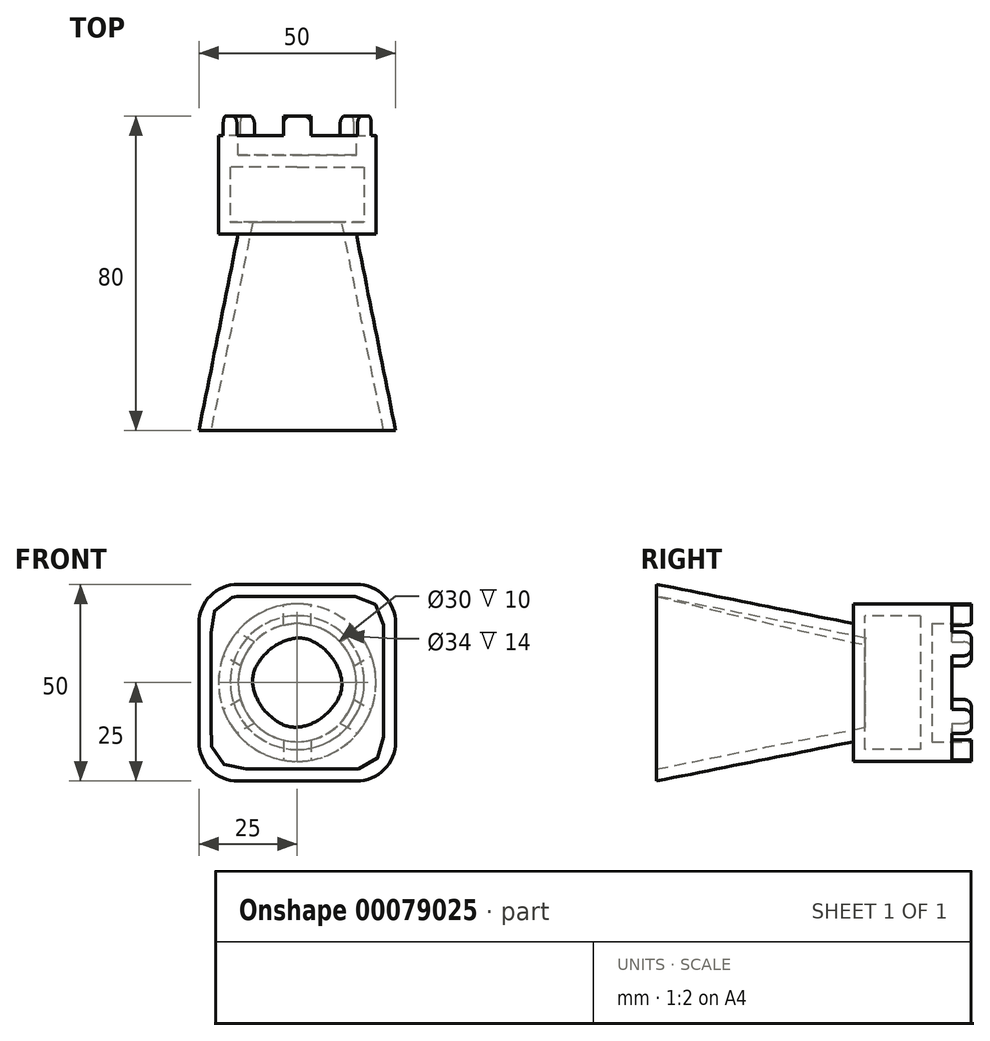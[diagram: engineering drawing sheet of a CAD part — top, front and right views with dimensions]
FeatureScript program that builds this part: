
annotation { "Feature Type Name" : "Feature", "Feature Type Description" : "" }
export const myFeature = defineFeature(function(context is Context, id is Id, definition is map)
    precondition{}
    {
        {
            var Q0;
            Q0=qCreatedBy(makeId("Front.planeOp"),FACE);
            var sketch = newSketch(context, id + "F0", { "sketchPlane" : qUnion([Q0])});
            skCircle(sketch, "E0", {"center": v(0, 0) * mm, "radius": 20 * mm});
            skSolve(sketch);
        }
        {
            var Q0;
            Q0=makeQuery(id+"F0.imprint","IMPRINT",FACE,{"disambiguationData":[TD([[makeQuery(id+"F0.imprint","IMPRINT",EDGE,{"derivedFrom":sQuery(id+"F0.wireOp",EDGE,"E0")}),1.0]])]});
            extrude(context, id + "F1", {"entities" : qUnion([Q0]), "oppositeDirection" : true, "depth" : 30 * mm});
        }
        {
            var Q0;
            Q0=makeQuery(id+"F1.opExtrude","CAP_FACE",FACE,{"disambiguationData":[OSD([sQuery(id+"F0.wireOp",EDGE,"E0")])],"isStart":false});
            var sketch = newSketch(context, id + "F2", { "sketchPlane" : qUnion([Q0])});
            skCircle(sketch, "E1", {"center": v(0, 0) * mm, "radius": 15 * mm});
            skSolve(sketch);
        }
        {
            var Q0;
            Q0 = qSketchRegion(id + "F2", true);
            extrude(context, id + "F3", {"entities" : qUnion([Q0]), "operationType" : NewBodyOperationType.REMOVE, "oppositeDirection" : true, "depth" : 10 * mm});
        }
        {
            var Q0;
            Q0=makeQuery(id+"F1.opExtrude","CAP_FACE",FACE,{"disambiguationData":[OSD([sQuery(id+"F0.wireOp",EDGE,"E0")])],"isStart":false});
            var sketch = newSketch(context, id + "F4", { "sketchPlane" : qUnion([Q0])});
            skLineSegment(sketch, "E2.bottom", {"start": v(-3.5, -14.59) * mm, "end": v(3.5, -14.59) * mm});
            skLineSegment(sketch, "E2.top", {"start": v(-3.5, -19.7) * mm, "end": v(3.5, -19.7) * mm, "construction": true});
            skLineSegment(sketch, "E2.left", {"start": v(-3.5, -14.59) * mm, "end": v(-3.5, -19.7) * mm});
            skLineSegment(sketch, "E2.right", {"start": v(3.5, -14.59) * mm, "end": v(3.5, -19.7) * mm});
            skLineSegment(sketch, "E3", {"start": v(0, -19.7) * mm, "end": v(0, 0) * mm, "construction": true});
            skArc(sketch, "E4", {"start": v(-3.5, -19.7) * mm, "mid": v(0, -20) * mm, "end": v(3.5, -19.7) * mm});
            skLineSegment(sketch, "E5.1.0", {"start": v(10.88, -10.32) * mm, "end": v(15.3, -12.88) * mm});
            skLineSegment(sketch, "E5.1.1", {"start": v(10.88, -10.32) * mm, "end": v(14.38, -4.26) * mm});
            skLineSegment(sketch, "E5.1.2", {"start": v(15.3, -12.88) * mm, "end": v(18.8, -6.81) * mm, "construction": true});
            skLineSegment(sketch, "E5.1.3", {"start": v(14.38, -4.26) * mm, "end": v(18.8, -6.81) * mm});
            skArc(sketch, "E5.1.4", {"start": v(15.3, -12.88) * mm, "mid": v(17.32, -10) * mm, "end": v(18.8, -6.81) * mm});
            skLineSegment(sketch, "E5.2.0", {"start": v(14.38, 4.26) * mm, "end": v(18.8, 6.81) * mm});
            skLineSegment(sketch, "E5.2.1", {"start": v(14.38, 4.26) * mm, "end": v(10.88, 10.32) * mm});
            skLineSegment(sketch, "E5.2.2", {"start": v(18.8, 6.81) * mm, "end": v(15.3, 12.88) * mm, "construction": true});
            skLineSegment(sketch, "E5.2.3", {"start": v(10.88, 10.32) * mm, "end": v(15.3, 12.88) * mm});
            skArc(sketch, "E5.2.4", {"start": v(18.8, 6.81) * mm, "mid": v(17.32, 10) * mm, "end": v(15.3, 12.88) * mm});
            skLineSegment(sketch, "E5.3.0", {"start": v(3.5, 14.59) * mm, "end": v(3.5, 19.7) * mm});
            skLineSegment(sketch, "E5.3.1", {"start": v(3.5, 14.59) * mm, "end": v(-3.5, 14.59) * mm});
            skLineSegment(sketch, "E5.3.2", {"start": v(3.5, 19.7) * mm, "end": v(-3.5, 19.7) * mm, "construction": true});
            skLineSegment(sketch, "E5.3.3", {"start": v(-3.5, 14.59) * mm, "end": v(-3.5, 19.7) * mm});
            skArc(sketch, "E5.3.4", {"start": v(3.5, 19.7) * mm, "mid": v(0, 20) * mm, "end": v(-3.5, 19.7) * mm});
            skLineSegment(sketch, "E5.4.0", {"start": v(-10.88, 10.32) * mm, "end": v(-15.3, 12.88) * mm});
            skLineSegment(sketch, "E5.4.1", {"start": v(-10.88, 10.32) * mm, "end": v(-14.38, 4.26) * mm});
            skLineSegment(sketch, "E5.4.2", {"start": v(-15.3, 12.88) * mm, "end": v(-18.8, 6.81) * mm, "construction": true});
            skLineSegment(sketch, "E5.4.3", {"start": v(-14.38, 4.26) * mm, "end": v(-18.8, 6.81) * mm});
            skArc(sketch, "E5.4.4", {"start": v(-15.3, 12.88) * mm, "mid": v(-17.32, 10) * mm, "end": v(-18.8, 6.81) * mm});
            skLineSegment(sketch, "E5.5.0", {"start": v(-14.38, -4.26) * mm, "end": v(-18.8, -6.81) * mm});
            skLineSegment(sketch, "E5.5.1", {"start": v(-14.38, -4.26) * mm, "end": v(-10.88, -10.32) * mm});
            skLineSegment(sketch, "E5.5.2", {"start": v(-18.8, -6.81) * mm, "end": v(-15.3, -12.88) * mm, "construction": true});
            skLineSegment(sketch, "E5.5.3", {"start": v(-10.88, -10.32) * mm, "end": v(-15.3, -12.88) * mm});
            skArc(sketch, "E5.5.4", {"start": v(-18.8, -6.81) * mm, "mid": v(-17.32, -10) * mm, "end": v(-15.3, -12.88) * mm});
            skSolve(sketch);
        }
        {
            var Q0;
            {var subQ0=sQuery(id+"F4.wireOp",EDGE,"E2.left");var subQ3=makeQuery(id+"F1.opExtrude","CAP_EDGE",EDGE,{"disambiguationData":[OSD([sQuery(id+"F0.wireOp",EDGE,"E0")])],"isStart":false});var subQ4=makeQuery(id+"F4.imprint","INTERSECT",VERTEX,{"derivedFrom":[subQ3,subQ0]});Q0=makeQuery(id+"F4.imprint","IMPRINT",FACE,{"disambiguationData":[TD([[makeQuery(id+"F4.imprint","IMPRINT",EDGE,{"disambiguationData":[TD([[subQ4,1.0]])],"derivedFrom":subQ0}),-1.0]])]});}
            var Q1;
            {var subQ0=sQuery(id+"F4.wireOp",EDGE,"E5.4.3");Q1=makeQuery(id+"F4.imprint","IMPRINT",FACE,{"disambiguationData":[TD([[makeQuery(id+"F4.imprint","IMPRINT",EDGE,{"derivedFrom":subQ0}),1.0]])]});}
            var Q2;
            {var subQ0=sQuery(id+"F4.wireOp",EDGE,"E5.3.3");Q2=makeQuery(id+"F4.imprint","IMPRINT",FACE,{"disambiguationData":[TD([[makeQuery(id+"F4.imprint","IMPRINT",EDGE,{"derivedFrom":subQ0}),1.0]])]});}
            var Q3;
            {var subQ0=sQuery(id+"F4.wireOp",EDGE,"E5.2.3");Q3=makeQuery(id+"F4.imprint","IMPRINT",FACE,{"disambiguationData":[TD([[makeQuery(id+"F4.imprint","IMPRINT",EDGE,{"derivedFrom":subQ0}),1.0]])]});}
            var Q4;
            {var subQ0=sQuery(id+"F4.wireOp",EDGE,"E5.1.3");Q4=makeQuery(id+"F4.imprint","IMPRINT",FACE,{"disambiguationData":[TD([[makeQuery(id+"F4.imprint","IMPRINT",EDGE,{"derivedFrom":subQ0}),1.0]])]});}
            var Q5;
            {var subQ0=sQuery(id+"F4.wireOp",EDGE,"E2.right");Q5=makeQuery(id+"F4.imprint","IMPRINT",FACE,{"disambiguationData":[TD([[makeQuery(id+"F4.imprint","IMPRINT",EDGE,{"derivedFrom":subQ0}),1.0]])]});}
            extrude(context, id + "F5", {"entities" : qUnion([Q0, Q1, Q2, Q3, Q4, Q5]), "operationType" : NewBodyOperationType.REMOVE, "oppositeDirection" : true, "depth" : 5 * mm});
        }
        {
            var Q0;
            Q0=makeQuery(id+"F5.boolean.opBoolean","COPY",EDGE,{"derivedFrom":makeQuery(id+"F5.opExtrude","CAP_EDGE",EDGE,{"disambiguationData":[OSD([sQuery(id+"F4.wireOp",EDGE,"E2.right")])],"isStart":true})});
            var Q1;
            Q1=makeQuery(id+"F5.boolean.opBoolean","COPY",EDGE,{"derivedFrom":makeQuery(id+"F5.opExtrude","CAP_EDGE",EDGE,{"disambiguationData":[OSD([sQuery(id+"F4.wireOp",EDGE,"E2.left")])],"isStart":true})});
            var Q2;
            Q2=makeQuery(id+"F5.boolean.opBoolean","COPY",EDGE,{"derivedFrom":makeQuery(id+"F5.opExtrude","CAP_EDGE",EDGE,{"disambiguationData":[OSD([sQuery(id+"F4.wireOp",EDGE,"E5.5.3")])],"isStart":true})});
            var Q3;
            Q3=makeQuery(id+"F5.boolean.opBoolean","COPY",EDGE,{"derivedFrom":makeQuery(id+"F5.opExtrude","CAP_EDGE",EDGE,{"disambiguationData":[OSD([sQuery(id+"F4.wireOp",EDGE,"E5.5.0")])],"isStart":true})});
            var Q4;
            Q4=makeQuery(id+"F5.boolean.opBoolean","COPY",EDGE,{"derivedFrom":makeQuery(id+"F5.opExtrude","CAP_EDGE",EDGE,{"disambiguationData":[OSD([sQuery(id+"F4.wireOp",EDGE,"E5.4.3")])],"isStart":true})});
            var Q5;
            Q5=makeQuery(id+"F5.boolean.opBoolean","COPY",EDGE,{"derivedFrom":makeQuery(id+"F5.opExtrude","CAP_EDGE",EDGE,{"disambiguationData":[OSD([sQuery(id+"F4.wireOp",EDGE,"E5.3.3")])],"isStart":true})});
            var Q6;
            Q6=makeQuery(id+"F5.boolean.opBoolean","COPY",EDGE,{"derivedFrom":makeQuery(id+"F5.opExtrude","CAP_EDGE",EDGE,{"disambiguationData":[OSD([sQuery(id+"F4.wireOp",EDGE,"E5.3.0")])],"isStart":true})});
            var Q7;
            Q7=makeQuery(id+"F5.boolean.opBoolean","COPY",EDGE,{"derivedFrom":makeQuery(id+"F5.opExtrude","CAP_EDGE",EDGE,{"disambiguationData":[OSD([sQuery(id+"F4.wireOp",EDGE,"E5.2.3")])],"isStart":true})});
            var Q8;
            Q8=makeQuery(id+"F5.boolean.opBoolean","COPY",EDGE,{"derivedFrom":makeQuery(id+"F5.opExtrude","CAP_EDGE",EDGE,{"disambiguationData":[OSD([sQuery(id+"F4.wireOp",EDGE,"E5.2.0")])],"isStart":true})});
            var Q9;
            Q9=makeQuery(id+"F5.boolean.opBoolean","COPY",EDGE,{"derivedFrom":makeQuery(id+"F5.opExtrude","CAP_EDGE",EDGE,{"disambiguationData":[OSD([sQuery(id+"F4.wireOp",EDGE,"E5.1.3")])],"isStart":true})});
            var Q10;
            Q10=makeQuery(id+"F5.boolean.opBoolean","COPY",EDGE,{"derivedFrom":makeQuery(id+"F5.opExtrude","CAP_EDGE",EDGE,{"disambiguationData":[OSD([sQuery(id+"F4.wireOp",EDGE,"E5.1.0")])],"isStart":true})});
            var Q11;
            Q11=makeQuery(id+"F5.boolean.opBoolean","COPY",EDGE,{"derivedFrom":makeQuery(id+"F5.opExtrude","CAP_EDGE",EDGE,{"disambiguationData":[OSD([sQuery(id+"F4.wireOp",EDGE,"E5.4.0")])],"isStart":true})});
            fillet(context, id + "F6", {"entities" : qUnion([Q0, Q1, Q2, Q3, Q4, Q5, Q6, Q7, Q8, Q9, Q10, Q11]), "radius" : 2 * mm, "tangentPropagation" : true, "allowEdgeOverflow" : false});
        }
        {
            var Q0;
            Q0=makeQuery(id+"F1.opExtrude","CAP_FACE",FACE,{"disambiguationData":[OSD([sQuery(id+"F0.wireOp",EDGE,"E0")])],"isStart":true});
            var sketch = newSketch(context, id + "F7", { "sketchPlane" : qUnion([Q0])});
            skCircle(sketch, "E6", {"center": v(0, 0) * mm, "radius": 15 * mm});
            skSolve(sketch);
        }
        {
            var Q0;
            Q0=makeQuery(id+"F7.imprint","IMPRINT",FACE,{"disambiguationData":[TD([[makeQuery(id+"F7.imprint","IMPRINT",EDGE,{"derivedFrom":sQuery(id+"F7.wireOp",EDGE,"E6")}),-1.0]])]});
            cPlane(context, id + "F8", {"entities" : qUnion([Q0]), "cplaneType" : CPlaneType.OFFSET, "offset" : 50 * mm, "width" : 150 * mm, "height" : 150 * mm});
        }
        {
            var Q0;
            Q0=qCreatedBy(id+"F8.planeOp",FACE);
            var sketch = newSketch(context, id + "F9", { "sketchPlane" : qUnion([Q0])});
            skLineSegment(sketch, "E7.bottom", {"start": v(15, 25) * mm, "end": v(-15, 25) * mm});
            skLineSegment(sketch, "E7.top", {"start": v(15, -25) * mm, "end": v(-15, -25) * mm});
            skLineSegment(sketch, "E7.left", {"start": v(25, 15) * mm, "end": v(25, -15) * mm});
            skLineSegment(sketch, "E7.right", {"start": v(-25, 15) * mm, "end": v(-25, -15) * mm});
            skPoint(sketch, "E7.middle", {"position": v(0, 0) * mm});
            skPoint(sketch, "E8.visualSharp", {"position": v(25, 25) * mm});
            skArc(sketch, "E8.filletArc", {"start": v(25, 15) * mm, "mid": v(22.07, 22.07) * mm, "end": v(15, 25) * mm});
            skPoint(sketch, "E9.visualSharp", {"position": v(-25, 25) * mm});
            skArc(sketch, "E9.filletArc", {"start": v(-15, 25) * mm, "mid": v(-22.07, 22.07) * mm, "end": v(-25, 15) * mm});
            skPoint(sketch, "E10.visualSharp", {"position": v(-25, -25) * mm});
            skArc(sketch, "E10.filletArc", {"start": v(-25, -15) * mm, "mid": v(-22.07, -22.07) * mm, "end": v(-15, -25) * mm});
            skPoint(sketch, "E11.visualSharp", {"position": v(25, -25) * mm});
            skArc(sketch, "E11.filletArc", {"start": v(15, -25) * mm, "mid": v(22.07, -22.07) * mm, "end": v(25, -15) * mm});
            skSolve(sketch);
        }
        {
            var Q1;
            Q1=makeQuery(id+"F9.imprint","IMPRINT",FACE,{"disambiguationData":[TD([[makeQuery(id+"F9.imprint","IMPRINT",EDGE,{"derivedFrom":sQuery(id+"F9.wireOp",EDGE,"E7.bottom")}),1.0]])]});
            var Q2;
            Q2=makeQuery(id+"F7.imprint","IMPRINT",FACE,{"disambiguationData":[TD([[makeQuery(id+"F7.imprint","IMPRINT",EDGE,{"derivedFrom":sQuery(id+"F7.wireOp",EDGE,"E6")}),1.0]])]});
            loft(context, id + "F10", {"operationType" : NewBodyOperationType.ADD, "sheetProfilesArray" : [{ "sheetProfileEntities" : qUnion([Q1]) }, { "sheetProfileEntities" : qUnion([Q2]) }]});
        }
        {
            var Q0;
            Q0=makeQuery(id+"F10.opLoft","CAP_FACE",FACE,{"disambiguationData":[OSD([makeQuery(id+"F9.imprint","IMPRINT",FACE,{"disambiguationData":[TD([[makeQuery(id+"F9.imprint","IMPRINT",EDGE,{"derivedFrom":sQuery(id+"F9.wireOp",EDGE,"E7.bottom")}),1.0]])]})])],"isStart":true});
            shell(context, id + "F11", {"entities" : qUnion([Q0]), "thickness" : 3 * mm});
        }
    });
